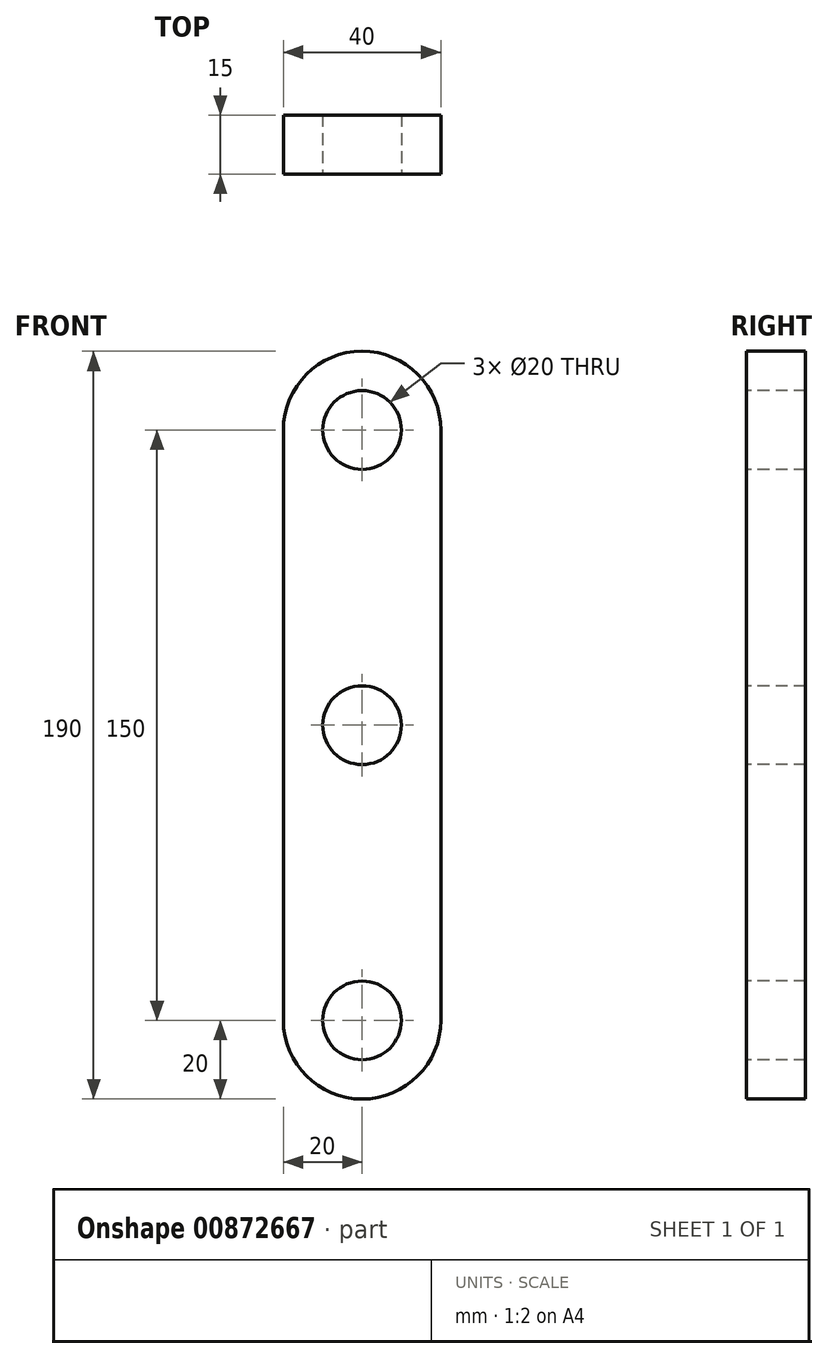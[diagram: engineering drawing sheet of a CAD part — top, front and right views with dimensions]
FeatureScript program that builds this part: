
annotation { "Feature Type Name" : "Feature", "Feature Type Description" : "" }
export const myFeature = defineFeature(function(context is Context, id is Id, definition is map)
    precondition{}
    {
        {
            var Q0;
            Q0=qCreatedBy(makeId("Front.planeOp"),FACE);
            var sketch = newSketch(context, id + "F0", { "sketchPlane" : qUnion([Q0])});
            skCircle(sketch, "E0", {"center": v(0, 0) * mm, "radius": 20 * mm});
            skCircle(sketch, "E1", {"center": v(0, 150) * mm, "radius": 20 * mm});
            skLineSegment(sketch, "E2", {"start": v(-20, 150) * mm, "end": v(-20, 0) * mm});
            skLineSegment(sketch, "E3", {"start": v(20, 150) * mm, "end": v(20, 0) * mm});
            skSolve(sketch);
        }
        {
            var Q0;
            Q0 = qSketchRegion(id + "F0", true);
            extrude(context, id + "F1", {"entities" : qUnion([Q0]), "depth" : 15 * mm, "offsetDistance" : 25 * mm});
        }
        {
            var Q0;
            Q0=makeQuery(id+"F1.opExtrude","CAP_FACE",FACE,{"disambiguationData":[OSD([sQuery(id+"F0.wireOp",EDGE,"E0"),sQuery(id+"F0.wireOp",EDGE,"E1"),sQuery(id+"F0.wireOp",EDGE,"E2"),sQuery(id+"F0.wireOp",EDGE,"E3")])],"isStart":false});
            var sketch = newSketch(context, id + "F2", { "sketchPlane" : qUnion([Q0])});
            skCircle(sketch, "E4", {"center": v(0, 0) * mm, "radius": 10 * mm});
            skCircle(sketch, "E5", {"center": v(0, 150) * mm, "radius": 10 * mm});
            skSolve(sketch);
        }
        {
            var Q0;
            Q0=makeQuery(id+"F2.imprint","IMPRINT",FACE,{"disambiguationData":[TD([[makeQuery(id+"F2.imprint","IMPRINT",EDGE,{"derivedFrom":sQuery(id+"F2.wireOp",EDGE,"E5")}),1.0]])]});
            var Q1;
            Q1=makeQuery(id+"F2.imprint","IMPRINT",FACE,{"disambiguationData":[TD([[makeQuery(id+"F2.imprint","IMPRINT",EDGE,{"derivedFrom":sQuery(id+"F2.wireOp",EDGE,"E4")}),1.0]])]});
            extrude(context, id + "F3", {"entities" : qUnion([Q0, Q1]), "operationType" : NewBodyOperationType.REMOVE, "oppositeDirection" : true, "depth" : 25 * mm, "offsetDistance" : 25 * mm});
        }
        {
            var Q0;
            Q0=makeQuery(id+"F1.opExtrude","CAP_FACE",FACE,{"disambiguationData":[OSD([sQuery(id+"F0.wireOp",EDGE,"E0"),sQuery(id+"F0.wireOp",EDGE,"E1"),sQuery(id+"F0.wireOp",EDGE,"E2"),sQuery(id+"F0.wireOp",EDGE,"E3")])],"isStart":false});
            var sketch = newSketch(context, id + "F4", { "sketchPlane" : qUnion([Q0])});
            skCircle(sketch, "E6", {"center": v(0, 75) * mm, "radius": 10 * mm});
            skSolve(sketch);
        }
        {
            var Q0;
            Q0=makeQuery(id+"F4.imprint","IMPRINT",FACE,{"disambiguationData":[TD([[makeQuery(id+"F4.imprint","IMPRINT",EDGE,{"derivedFrom":sQuery(id+"F4.wireOp",EDGE,"E6")}),1.0]])]});
            extrude(context, id + "F5", {"entities" : qUnion([Q0]), "operationType" : NewBodyOperationType.REMOVE, "oppositeDirection" : true, "depth" : 25 * mm, "offsetDistance" : 25 * mm});
        }
    });
